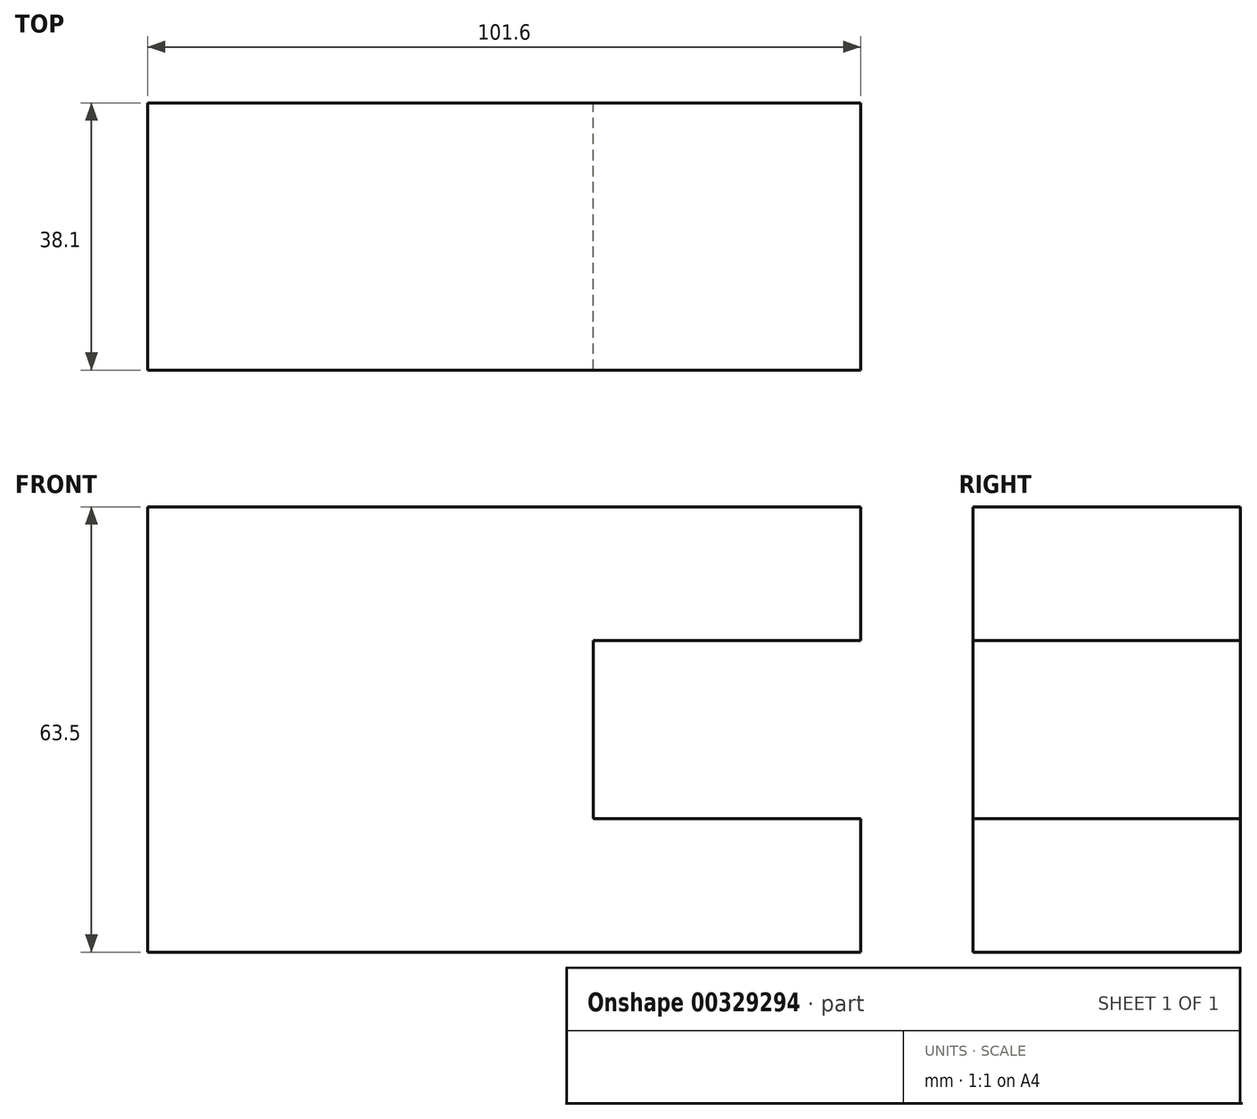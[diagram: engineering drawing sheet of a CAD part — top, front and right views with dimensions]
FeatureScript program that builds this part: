
annotation { "Feature Type Name" : "Feature", "Feature Type Description" : "" }
export const myFeature = defineFeature(function(context is Context, id is Id, definition is map)
    precondition{}
    {
        {
            var Q0;
            Q0=qCreatedBy(makeId("Front.planeOp"),FACE);
            var sketch = newSketch(context, id + "F0", { "sketchPlane" : qUnion([Q0])});
            skLineSegment(sketch, "E0", {"start": v(-70.83, 44.45) * mm, "end": v(30.77, 44.45) * mm});
            skLineSegment(sketch, "E1", {"start": v(-70.83, 44.45) * mm, "end": v(-70.83, -19.05) * mm});
            skLineSegment(sketch, "E2", {"start": v(-70.83, -19.05) * mm, "end": v(30.77, -19.05) * mm});
            skLineSegment(sketch, "E3", {"start": v(30.77, -19.05) * mm, "end": v(30.77, 0) * mm});
            skLineSegment(sketch, "E4", {"start": v(30.77, 0) * mm, "end": v(-7.33, 0) * mm});
            skLineSegment(sketch, "E5", {"start": v(-7.33, 0) * mm, "end": v(-7.33, 25.4) * mm});
            skLineSegment(sketch, "E6", {"start": v(-7.33, 25.4) * mm, "end": v(30.77, 25.4) * mm});
            skLineSegment(sketch, "E7", {"start": v(30.77, 25.4) * mm, "end": v(30.77, 44.45) * mm});
            skSolve(sketch);
        }
        {
            var Q0;
            Q0 = qSketchRegion(id + "F0", true);
            extrude(context, id + "F1", {"entities" : qUnion([Q0]), "depth" : 38.1 * mm});
        }
    });
